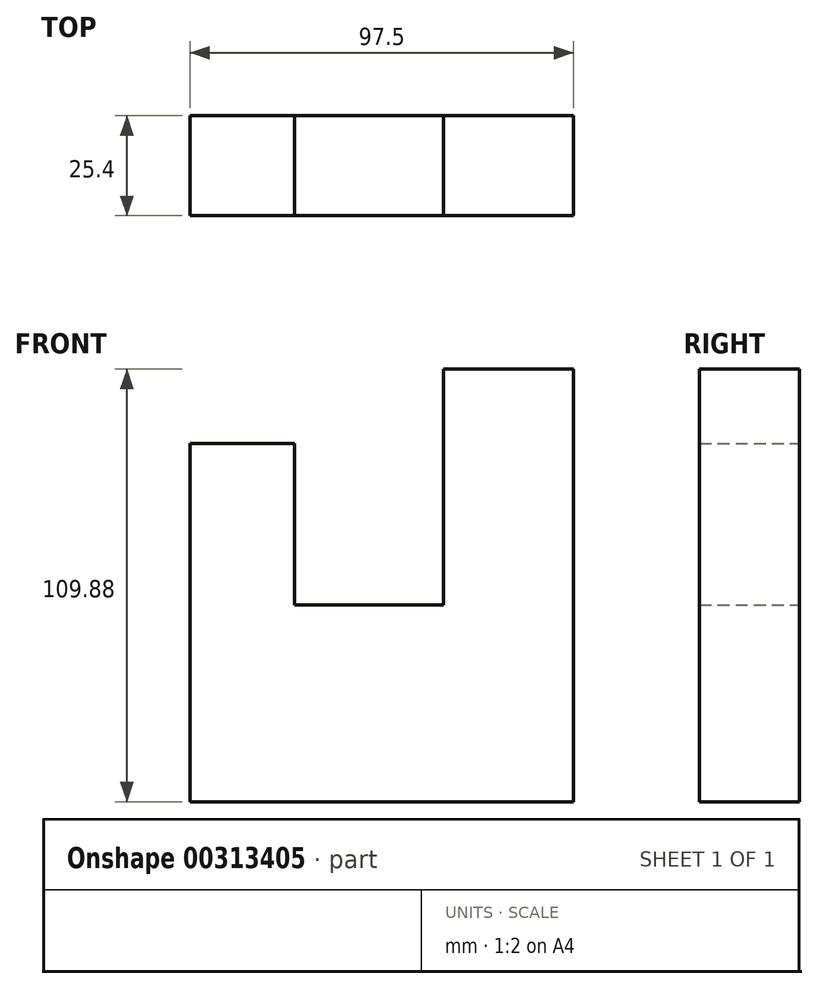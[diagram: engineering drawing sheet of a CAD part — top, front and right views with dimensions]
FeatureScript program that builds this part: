
annotation { "Feature Type Name" : "Feature", "Feature Type Description" : "" }
export const myFeature = defineFeature(function(context is Context, id is Id, definition is map)
    precondition{}
    {
        {
            var Q0;
            Q0=qCreatedBy(makeId("Front.planeOp"),FACE);
            var sketch = newSketch(context, id + "F0", { "sketchPlane" : qUnion([Q0])});
            skLineSegment(sketch, "E0", {"start": v(-49.52, 23.99) * mm, "end": v(-49.52, -49.99) * mm});
            skLineSegment(sketch, "E1", {"start": v(-49.52, -49.99) * mm, "end": v(47.98, -49.99) * mm});
            skLineSegment(sketch, "E2", {"start": v(47.98, -49.99) * mm, "end": v(47.98, 59.9) * mm});
            skLineSegment(sketch, "E3", {"start": v(47.98, 59.9) * mm, "end": v(14.86, 59.9) * mm});
            skLineSegment(sketch, "E4", {"start": v(14.86, 59.9) * mm, "end": v(14.86, 0) * mm});
            skLineSegment(sketch, "E5", {"start": v(14.86, 0) * mm, "end": v(-22.9, 0) * mm});
            skLineSegment(sketch, "E6", {"start": v(-22.9, 0) * mm, "end": v(-22.9, 41.01) * mm});
            skLineSegment(sketch, "E7", {"start": v(-22.9, 41.01) * mm, "end": v(-49.52, 41.01) * mm});
            skLineSegment(sketch, "E8", {"start": v(-49.52, 41.01) * mm, "end": v(-49.52, 23.99) * mm});
            skSolve(sketch);
        }
        {
            var Q0;
            Q0=makeQuery(id+"F0.imprint","IMPRINT",FACE,{"disambiguationData":[TD([[makeQuery(id+"F0.imprint","IMPRINT",EDGE,{"derivedFrom":sQuery(id+"F0.wireOp",EDGE,"E0")}),1.0]])]});
            extrude(context, id + "F1", {"entities" : qUnion([Q0]), "depth" : 25.4 * mm});
        }
    });
